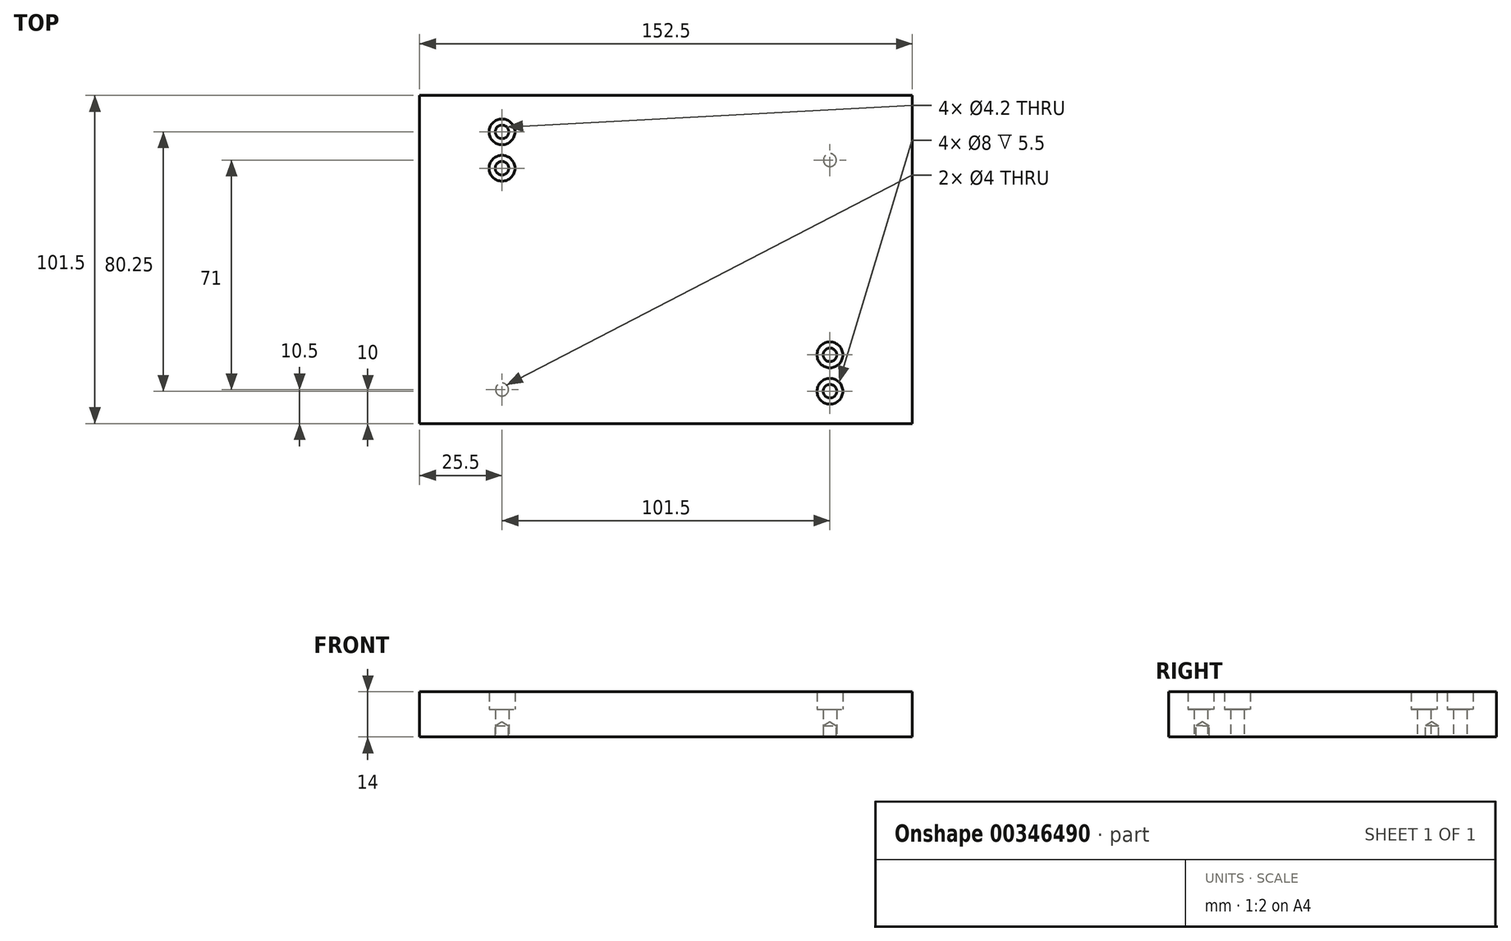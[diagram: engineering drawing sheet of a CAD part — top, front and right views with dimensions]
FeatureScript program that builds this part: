
annotation { "Feature Type Name" : "Feature", "Feature Type Description" : "" }
export const myFeature = defineFeature(function(context is Context, id is Id, definition is map)
    precondition{}
    {
        {
            var Q0;
            Q0=qCreatedBy(makeId("Top.planeOp"),FACE);
            var sketch = newSketch(context, id + "F0", { "sketchPlane" : qUnion([Q0])});
            skLineSegment(sketch, "E0.bottom", {"start": v(0, 0) * mm, "end": v(152.5, 0) * mm});
            skLineSegment(sketch, "E0.top", {"start": v(0, 101.5) * mm, "end": v(152.5, 101.5) * mm});
            skLineSegment(sketch, "E0.left", {"start": v(0, 0) * mm, "end": v(0, 101.5) * mm});
            skLineSegment(sketch, "E0.right", {"start": v(152.5, 0) * mm, "end": v(152.5, 101.5) * mm});
            skPoint(sketch, "E1", {"position": v(25.5, 79) * mm});
            skPoint(sketch, "E2", {"position": v(127, 10) * mm});
            skPoint(sketch, "E3", {"position": v(127, 21.25) * mm});
            skPoint(sketch, "E4", {"position": v(25.5, 90.25) * mm});
            skSolve(sketch);
        }
        {
            var Q0;
            Q0=makeQuery(id+"F0.imprint","IMPRINT",FACE,{"disambiguationData":[TD([[makeQuery(id+"F0.imprint","IMPRINT",EDGE,{"derivedFrom":sQuery(id+"F0.wireOp",EDGE,"E0.bottom")}),1.0]])]});
            extrude(context, id + "F1", {"entities" : qUnion([Q0]), "depth" : -14 * mm});
        }
        {
            var Q0;
            Q0=sQuery(id+"F0.wireOp",VERTEX,"E2");
            var Q1;
            Q1=sQuery(id+"F0.wireOp",VERTEX,"E3");
            var Q2;
            Q2=sQuery(id+"F0.wireOp",VERTEX,"E4");
            var Q3;
            Q3=sQuery(id+"F0.wireOp",VERTEX,"E1");
            var Q4;
            Q4=makeQuery(id+"F1.opExtrude","SWEPT_BODY",BODY,{"disambiguationData":[OSD([sQuery(id+"F0.wireOp",EDGE,"E0.bottom"),sQuery(id+"F0.wireOp",EDGE,"E0.top"),sQuery(id+"F0.wireOp",EDGE,"E0.left"),sQuery(id+"F0.wireOp",EDGE,"E0.right")])]});
            hole(context, id + "F2", {"style" : HoleStyle.C_BORE, "endStyle" : HoleEndStyle.THROUGH, "holeDiameter" : 4.2 * mm, "cBoreDiameter" : 8 * mm, "cBoreDepth" : 5.5 * mm, "isTappedThrough" : true, "tappedDepth" : 7.75 * mm, "tapClearance" : 3, "locations" : qUnion([Q0, Q1, Q2, Q3]), "scope" : qUnion([Q4])});
        }
        {
            var Q0;
            Q0=makeQuery(id+"F1.opExtrude","CAP_FACE",FACE,{"disambiguationData":[OSD([sQuery(id+"F0.wireOp",EDGE,"E0.bottom"),sQuery(id+"F0.wireOp",EDGE,"E0.top"),sQuery(id+"F0.wireOp",EDGE,"E0.left"),sQuery(id+"F0.wireOp",EDGE,"E0.right")])],"isStart":false});
            var sketch = newSketch(context, id + "F3", { "sketchPlane" : qUnion([Q0])});
            skPoint(sketch, "E5", {"position": v(25.5, -10.5) * mm});
            skPoint(sketch, "E6", {"position": v(127, -81.5) * mm});
            skSolve(sketch);
        }
        {
            var Q0;
            Q0=sQuery(id+"F3.wireOp",VERTEX,"E5");
            var Q1;
            Q1=sQuery(id+"F3.wireOp",VERTEX,"E6");
            var Q2;
            Q2=makeQuery(id+"F1.opExtrude","SWEPT_BODY",BODY,{"disambiguationData":[OSD([sQuery(id+"F0.wireOp",EDGE,"E0.bottom"),sQuery(id+"F0.wireOp",EDGE,"E0.top"),sQuery(id+"F0.wireOp",EDGE,"E0.left"),sQuery(id+"F0.wireOp",EDGE,"E0.right")])]});
            hole(context, id + "F4", {"style" : HoleStyle.SIMPLE, "endStyle" : HoleEndStyle.BLIND, "holeDiameter" : 4 * mm, "holeDepth" : 3.5 * mm, "isTappedThrough" : true, "tappedDepth" : 7.75 * mm, "tapClearance" : 3, "locations" : qUnion([Q0, Q1]), "scope" : qUnion([Q2])});
        }
    });
